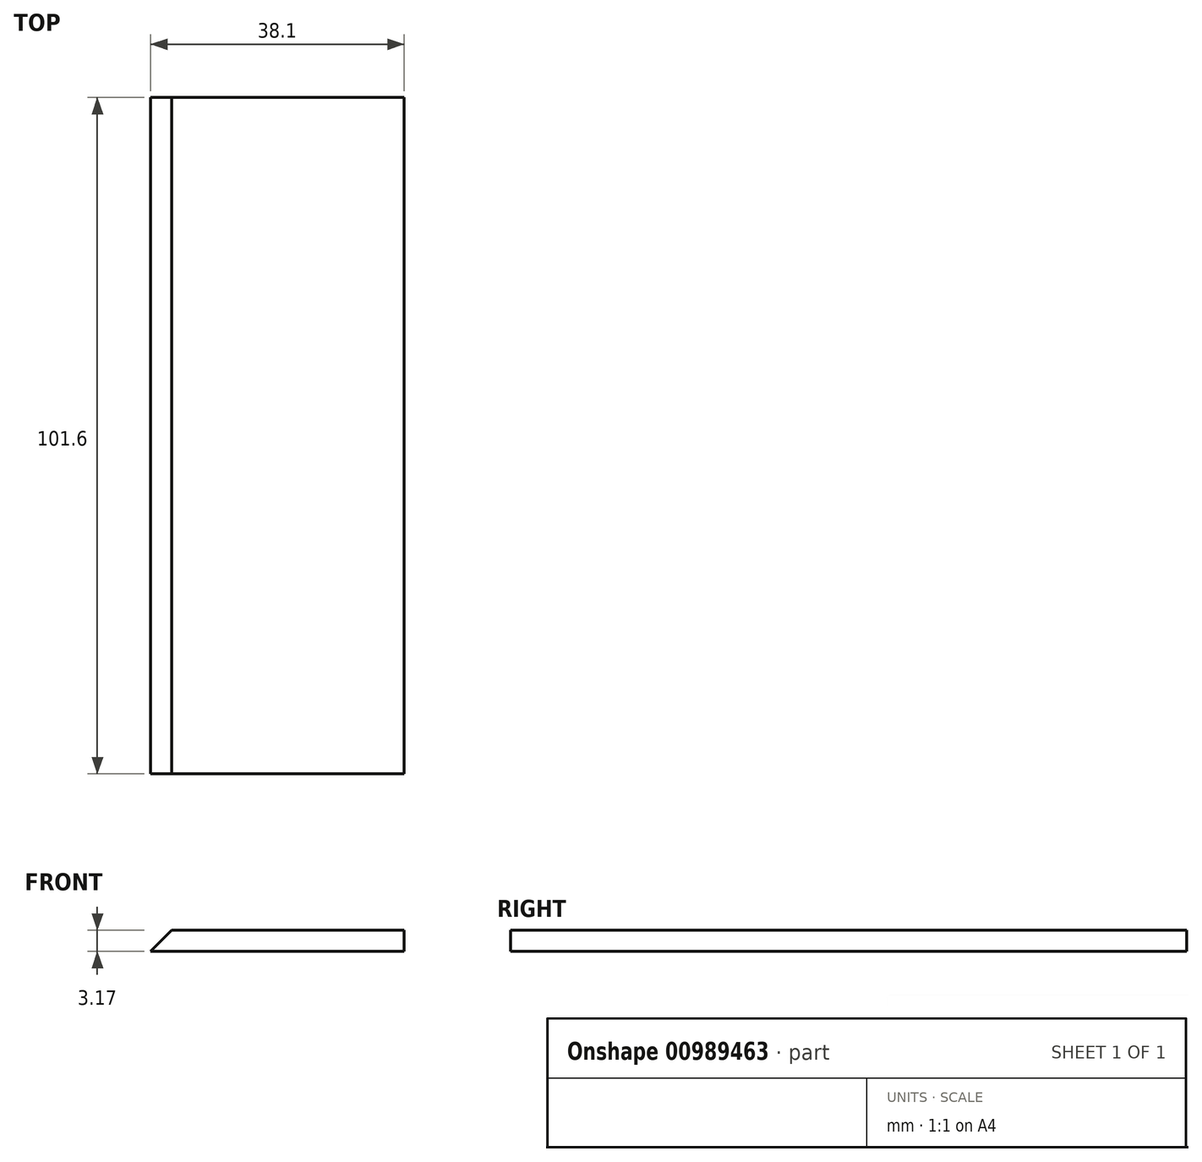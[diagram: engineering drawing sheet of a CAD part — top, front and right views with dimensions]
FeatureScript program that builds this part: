
annotation { "Feature Type Name" : "Feature", "Feature Type Description" : "" }
export const myFeature = defineFeature(function(context is Context, id is Id, definition is map)
    precondition{}
    {
        {
            var Q0;
            Q0=qCreatedBy(makeId("Front.planeOp"),FACE);
            var sketch = newSketch(context, id + "F0", { "sketchPlane" : qUnion([Q0])});
            skLineSegment(sketch, "E0.bottom", {"start": v(0.53, 1.32) * mm, "end": v(-34.4, 1.32) * mm});
            skLineSegment(sketch, "E0.top", {"start": v(0.53, -1.85) * mm, "end": v(-37.57, -1.85) * mm});
            skLineSegment(sketch, "E0.left", {"start": v(0.53, 1.32) * mm, "end": v(0.53, -1.85) * mm});
            skPoint(sketch, "E0.middle", {"position": v(-18.52, -0.26) * mm});
            skLineSegment(sketch, "E1", {"start": v(-37.57, -1.85) * mm, "end": v(-34.4, 1.32) * mm});
            skPoint(sketch, "E2.orphan", {"position": v(-37.57, 1.32) * mm});
            skSolve(sketch);
        }
        {
            var Q0;
            Q0 = qSketchRegion(id + "F0", true);
            extrude(context, id + "F1", {"entities" : qUnion([Q0]), "endBound" : BoundingType.SYMMETRIC, "depth" : 101.6 * mm, "offsetDistance" : 25.4 * mm});
        }
    });
